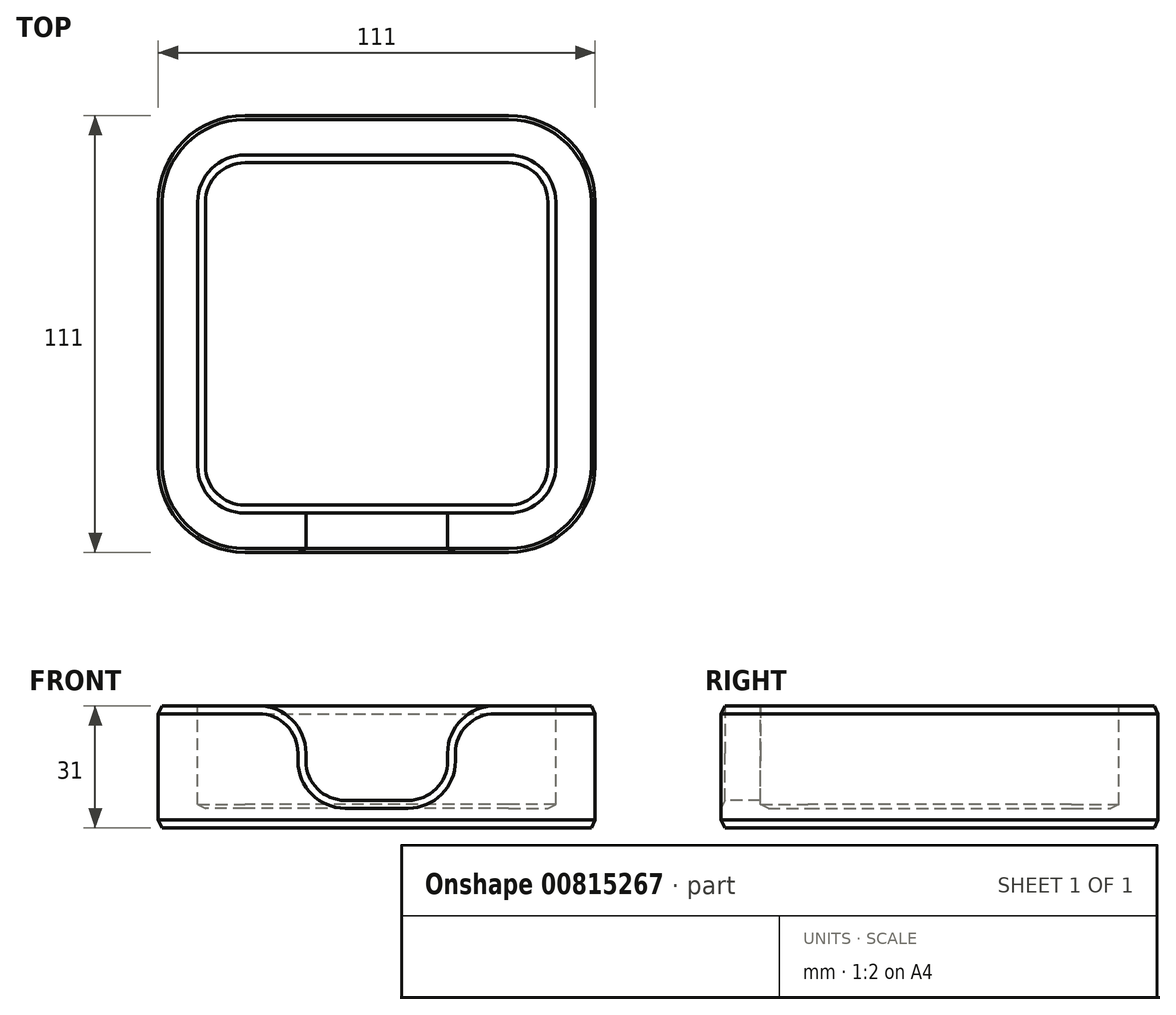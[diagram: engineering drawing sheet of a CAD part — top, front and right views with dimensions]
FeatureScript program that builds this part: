
annotation { "Feature Type Name" : "Feature", "Feature Type Description" : "" }
export const myFeature = defineFeature(function(context is Context, id is Id, definition is map)
    precondition{}
    {
        {
            var Q0;
            Q0=qCreatedBy(makeId("Top.planeOp"),FACE);
            var sketch = newSketch(context, id + "F0", { "sketchPlane" : qUnion([Q0])});
            skPoint(sketch, "E0.middle", {"position": v(0, 0) * mm});
            skLineSegment(sketch, "E1.bottom", {"start": v(33.5, 45.5) * mm, "end": v(-33.5, 45.5) * mm, "construction": true});
            skLineSegment(sketch, "E1.top", {"start": v(33.5, -45.5) * mm, "end": v(-33.5, -45.5) * mm, "construction": true});
            skLineSegment(sketch, "E1.left", {"start": v(45.5, 33.5) * mm, "end": v(45.5, -33.5) * mm, "construction": true});
            skLineSegment(sketch, "E1.right", {"start": v(-45.5, 33.5) * mm, "end": v(-45.5, -33.5) * mm, "construction": true});
            skPoint(sketch, "E2.visualSharp", {"position": v(-45.5, 45.5) * mm});
            skArc(sketch, "E2.filletArc", {"start": v(-33.5, 45.5) * mm, "mid": v(-41.99, 41.99) * mm, "end": v(-45.5, 33.5) * mm, "construction": true});
            skPoint(sketch, "E3.visualSharp", {"position": v(45.5, 45.5) * mm});
            skArc(sketch, "E3.filletArc", {"start": v(45.5, 33.5) * mm, "mid": v(41.99, 41.99) * mm, "end": v(33.5, 45.5) * mm, "construction": true});
            skPoint(sketch, "E4.visualSharp", {"position": v(45.5, -45.5) * mm});
            skArc(sketch, "E4.filletArc", {"start": v(33.5, -45.5) * mm, "mid": v(41.99, -41.99) * mm, "end": v(45.5, -33.5) * mm, "construction": true});
            skPoint(sketch, "E5.visualSharp", {"position": v(-45.5, -45.5) * mm});
            skArc(sketch, "E5.filletArc", {"start": v(-45.5, -33.5) * mm, "mid": v(-41.99, -41.99) * mm, "end": v(-33.5, -45.5) * mm, "construction": true});
            skArc(sketch, "E6.0", {"start": v(55.5, 33.5) * mm, "mid": v(49.06, 49.06) * mm, "end": v(33.5, 55.5) * mm});
            skLineSegment(sketch, "E6.1", {"start": v(33.5, 55.5) * mm, "end": v(-33.5, 55.5) * mm});
            skLineSegment(sketch, "E6.2", {"start": v(55.5, 33.5) * mm, "end": v(55.5, -33.5) * mm});
            skArc(sketch, "E6.3", {"start": v(-33.5, 55.5) * mm, "mid": v(-49.06, 49.06) * mm, "end": v(-55.5, 33.5) * mm});
            skArc(sketch, "E6.4", {"start": v(33.5, -55.5) * mm, "mid": v(49.06, -49.06) * mm, "end": v(55.5, -33.5) * mm});
            skLineSegment(sketch, "E6.5", {"start": v(33.5, -55.5) * mm, "end": v(-33.5, -55.5) * mm});
            skArc(sketch, "E6.6", {"start": v(-55.5, -33.5) * mm, "mid": v(-49.06, -49.06) * mm, "end": v(-33.5, -55.5) * mm});
            skLineSegment(sketch, "E6.7", {"start": v(-55.5, 33.5) * mm, "end": v(-55.5, -33.5) * mm});
            skSolve(sketch);
        }
        {
            var Q0;
            Q0=makeQuery(id+"F0.imprint","IMPRINT",FACE,{"disambiguationData":[TD([[makeQuery(id+"F0.imprint","IMPRINT",EDGE,{"derivedFrom":sQuery(id+"F0.wireOp",EDGE,"E6.0")}),1.0]])]});
            extrude(context, id + "F1", {"entities" : qUnion([Q0]), "depth" : 31 * mm, "offsetDistance" : 25 * mm});
        }
        {
            var Q0;
            Q0=makeQuery(id+"F1.opExtrude","CAP_FACE",FACE,{"disambiguationData":[OSD([sQuery(id+"F0.wireOp",EDGE,"E6.0"),sQuery(id+"F0.wireOp",EDGE,"E6.1"),sQuery(id+"F0.wireOp",EDGE,"E6.2"),sQuery(id+"F0.wireOp",EDGE,"E6.3"),sQuery(id+"F0.wireOp",EDGE,"E6.4"),sQuery(id+"F0.wireOp",EDGE,"E6.5"),sQuery(id+"F0.wireOp",EDGE,"E6.6"),sQuery(id+"F0.wireOp",EDGE,"E6.7")])],"isStart":false});
            var sketch = newSketch(context, id + "F2", { "sketchPlane" : qUnion([Q0])});
            skArc(sketch, "E7.0", {"start": v(-33.5, 45.5) * mm, "mid": v(-41.99, 41.99) * mm, "end": v(-45.5, 33.5) * mm});
            skLineSegment(sketch, "E7.1", {"start": v(33.5, 45.5) * mm, "end": v(-33.5, 45.5) * mm});
            skLineSegment(sketch, "E7.2", {"start": v(-45.5, 33.5) * mm, "end": v(-45.5, -33.5) * mm});
            skArc(sketch, "E7.3", {"start": v(45.5, 33.5) * mm, "mid": v(41.99, 41.99) * mm, "end": v(33.5, 45.5) * mm});
            skArc(sketch, "E7.4", {"start": v(-45.5, -33.5) * mm, "mid": v(-41.99, -41.99) * mm, "end": v(-33.5, -45.5) * mm});
            skLineSegment(sketch, "E7.5", {"start": v(33.5, -45.5) * mm, "end": v(-33.5, -45.5) * mm});
            skArc(sketch, "E7.6", {"start": v(33.5, -45.5) * mm, "mid": v(41.99, -41.99) * mm, "end": v(45.5, -33.5) * mm});
            skLineSegment(sketch, "E7.7", {"start": v(45.5, 33.5) * mm, "end": v(45.5, -33.5) * mm});
            skSolve(sketch);
        }
        {
            var Q0;
            Q0=makeQuery(id+"F2.imprint","IMPRINT",FACE,{"disambiguationData":[TD([[makeQuery(id+"F2.imprint","IMPRINT",EDGE,{"derivedFrom":sQuery(id+"F2.wireOp",EDGE,"E7.0")}),1.0]])]});
            var Q1;
            Q1=makeQuery(id+"F1.opExtrude","CAP_FACE",FACE,{"disambiguationData":[OSD([sQuery(id+"F0.wireOp",EDGE,"E6.0"),sQuery(id+"F0.wireOp",EDGE,"E6.1"),sQuery(id+"F0.wireOp",EDGE,"E6.2"),sQuery(id+"F0.wireOp",EDGE,"E6.3"),sQuery(id+"F0.wireOp",EDGE,"E6.4"),sQuery(id+"F0.wireOp",EDGE,"E6.5"),sQuery(id+"F0.wireOp",EDGE,"E6.6"),sQuery(id+"F0.wireOp",EDGE,"E6.7")])],"isStart":true});
            extrude(context, id + "F3", {"entities" : qUnion([Q0]), "operationType" : NewBodyOperationType.REMOVE, "endBound" : BoundingType.UP_TO_SURFACE, "oppositeDirection" : true, "depth" : 25 * mm, "endBoundEntityFace" : qUnion([Q1]), "hasOffset" : true, "offsetDistance" : 5 * mm});
        }
        {
            var Q0;
            Q0=makeQuery(id+"F1.opExtrude","SWEPT_FACE",FACE,{"disambiguationData":[OSD([sQuery(id+"F0.wireOp",EDGE,"E6.5")])]});
            var sketch = newSketch(context, id + "F4", { "sketchPlane" : qUnion([Q0])});
            skArc(sketch, "E8", {"start": v(-18, 19) * mm, "mid": v(-21.51, 27.49) * mm, "end": v(-30, 31) * mm});
            skArc(sketch, "E9", {"start": v(30, 31) * mm, "mid": v(21.51, 27.49) * mm, "end": v(18, 19) * mm});
            skLineSegment(sketch, "E10", {"start": v(-30, 31) * mm, "end": v(30, 31) * mm});
            skPoint(sketch, "E11", {"position": v(0, 31) * mm});
            skLineSegment(sketch, "E12", {"start": v(-18, 19) * mm, "end": v(-18, 17) * mm});
            skLineSegment(sketch, "E13", {"start": v(-8, 7) * mm, "end": v(8, 7) * mm});
            skLineSegment(sketch, "E14", {"start": v(18, 17) * mm, "end": v(18, 19) * mm});
            skPoint(sketch, "E15.visualSharp", {"position": v(-18, 7) * mm});
            skArc(sketch, "E15.filletArc", {"start": v(-18, 17) * mm, "mid": v(-15.07, 9.93) * mm, "end": v(-8, 7) * mm});
            skPoint(sketch, "E16.visualSharp", {"position": v(18, 7) * mm});
            skArc(sketch, "E16.filletArc", {"start": v(8, 7) * mm, "mid": v(15.07, 9.93) * mm, "end": v(18, 17) * mm});
            skSolve(sketch);
        }
        {
            var Q0;
            Q0=makeQuery(id+"F4.imprint","IMPRINT",FACE,{"disambiguationData":[TD([[makeQuery(id+"F4.imprint","IMPRINT",EDGE,{"derivedFrom":sQuery(id+"F4.wireOp",EDGE,"E8")}),-1.0]])]});
            extrude(context, id + "F5", {"entities" : qUnion([Q0]), "operationType" : NewBodyOperationType.REMOVE, "endBound" : BoundingType.UP_TO_NEXT, "oppositeDirection" : true, "depth" : 25 * mm, "offsetDistance" : 25 * mm});
        }
        {
            var Q0;
            Q0=makeQuery(id+"F3.boolean.opBoolean","COPY",EDGE,{"derivedFrom":makeQuery(id+"F3.opExtrude","CAP_EDGE",EDGE,{"disambiguationData":[OSD([sQuery(id+"F2.wireOp",EDGE,"E7.1")])],"isStart":true})});
            var Q1;
            Q1=makeQuery(id+"F1.opExtrude","CAP_EDGE",EDGE,{"disambiguationData":[OSD([sQuery(id+"F0.wireOp",EDGE,"E6.1")])],"isStart":false});
            var Q2;
            Q2=makeQuery(id+"F1.opExtrude","CAP_EDGE",EDGE,{"disambiguationData":[OSD([sQuery(id+"F0.wireOp",EDGE,"E6.5")])],"isStart":true});
            var Q3;
            Q3=makeQuery(id+"F3.boolean.opBoolean","COPY",EDGE,{"derivedFrom":makeQuery(id+"F3.opExtrude","CAP_EDGE",EDGE,{"disambiguationData":[OSD([sQuery(id+"F2.wireOp",EDGE,"E7.2")])],"isStart":false})});
            chamfer(context, id + "F6", {"entities" : qUnion([Q0, Q1, Q2, Q3]), "chamferType" : ChamferType.TWO_OFFSETS, "width1" : 2 * mm, "oppositeDirection" : true, "width2" : 1 * mm, "tangentPropagation" : true});
        }
    });
